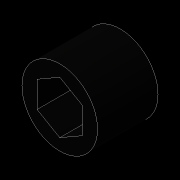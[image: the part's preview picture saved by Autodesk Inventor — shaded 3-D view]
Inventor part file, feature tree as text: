
AUTODESK INVENTOR PART (.ipt)
format: ipt  version: 2016 (Build 200138000, 138)  size: 80,384 bytes
history: native  units: in
note: dims shown in document units (in); Inventor stores cm internally (conversion verified against a paired STEP export)
features: extrude x1, sketch x1
ambient origin geometry x8: Origin, YZ Plane, XZ Plane, XY Plane, X Axis, Y Axis, Z Axis, Center Point
bodies: Solid1 (feature_tree)
feature tree (2):
  extrude  "Extrusion1"  Depth=0.5in
  sketch  "Sketch1"  dims[d0=0.375in d1=0.625in d2=0.5in d3=0.0in]
